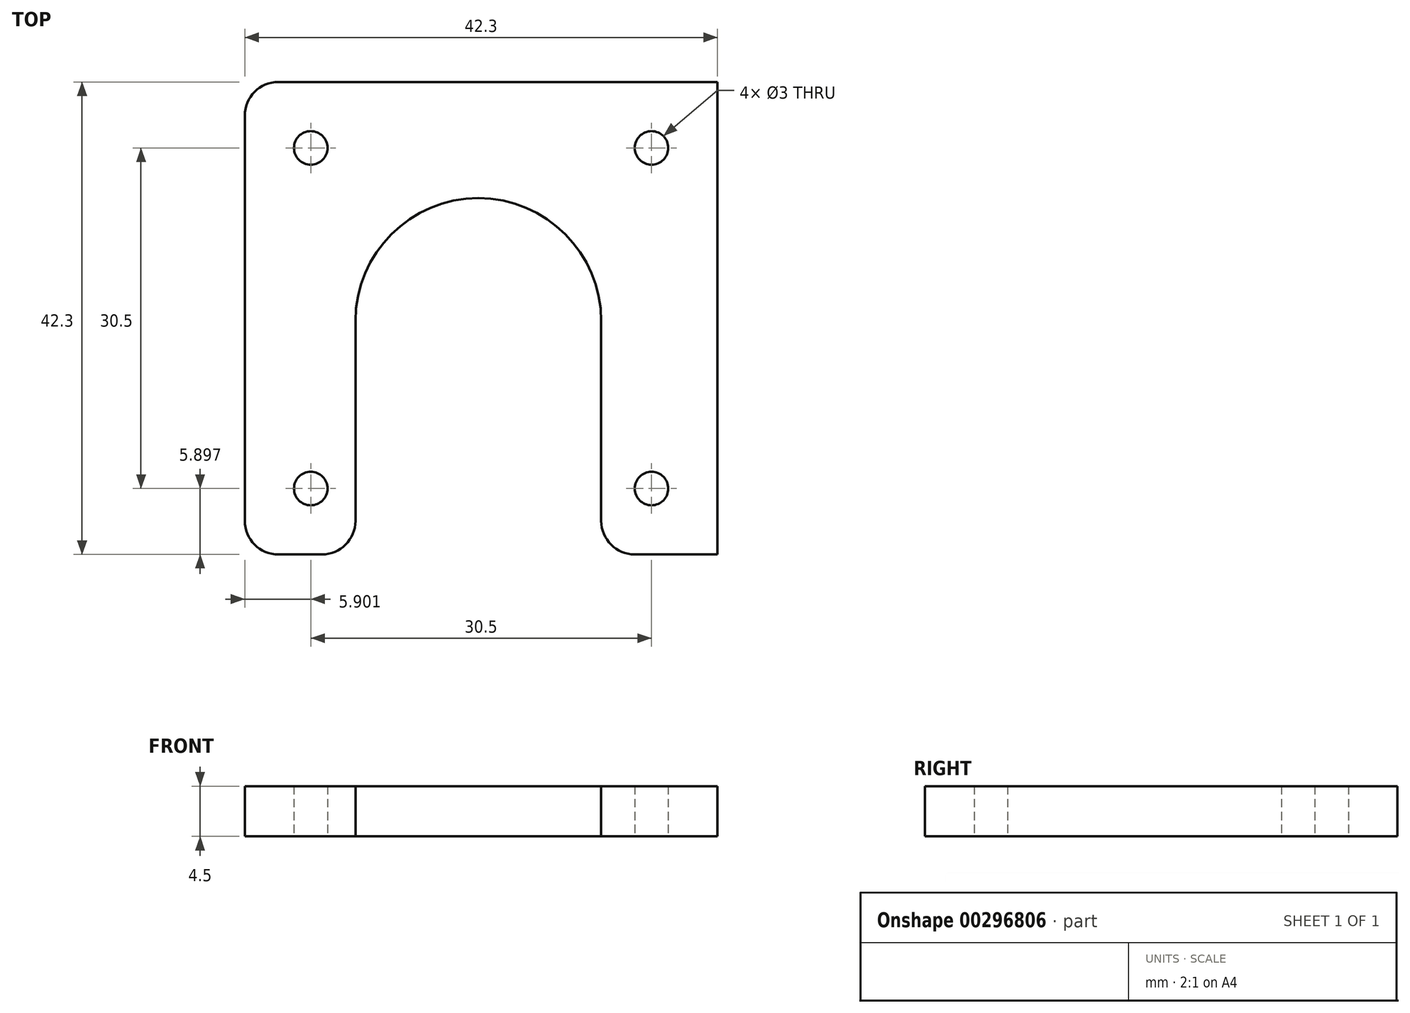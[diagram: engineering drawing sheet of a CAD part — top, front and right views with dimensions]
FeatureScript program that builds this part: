
annotation { "Feature Type Name" : "Feature", "Feature Type Description" : "" }
export const myFeature = defineFeature(function(context is Context, id is Id, definition is map)
    precondition{}
    {
        {
            var Q0;
            Q0=qCreatedBy(makeId("Top.planeOp"),FACE);
            var sketch = newSketch(context, id + "F0", { "sketchPlane" : qUnion([Q0])});
            skLineSegment(sketch, "E0.bottom", {"start": v(-20.2, 20.3) * mm, "end": v(22.1, 20.3) * mm});
            skLineSegment(sketch, "E0.top", {"start": v(-20.2, -22) * mm, "end": v(22.1, -22) * mm});
            skLineSegment(sketch, "E0.left", {"start": v(-20.2, 20.3) * mm, "end": v(-20.2, -22) * mm});
            skLineSegment(sketch, "E0.right", {"start": v(22.1, 20.3) * mm, "end": v(22.1, -22) * mm});
            skPoint(sketch, "E1", {"position": v(-14.3, 14.4) * mm});
            skPoint(sketch, "E2.0.1.0", {"position": v(-14.3, -16.1) * mm});
            skPoint(sketch, "E2.1.0.0", {"position": v(16.2, 14.4) * mm});
            skPoint(sketch, "E2.1.1.0", {"position": v(16.2, -16.1) * mm});
            skLineSegment(sketch, "E2.direction1", {"start": v(-14.3, 14.4) * mm, "end": v(16.2, 14.4) * mm, "construction": true});
            skLineSegment(sketch, "E2.direction2", {"start": v(-14.3, 14.4) * mm, "end": v(-14.3, -16.1) * mm, "construction": true});
            skCircle(sketch, "E3", {"center": v(-14.3, 14.4) * mm, "radius": 1.5 * mm});
            skCircle(sketch, "E4", {"center": v(16.2, 14.4) * mm, "radius": 1.5 * mm});
            skCircle(sketch, "E5", {"center": v(16.2, -16.1) * mm, "radius": 1.5 * mm});
            skCircle(sketch, "E6", {"center": v(-14.3, -16.1) * mm, "radius": 1.5 * mm});
            skCircle(sketch, "E7", {"center": v(0.7, -1.1) * mm, "radius": 2.5 * mm});
            skCircle(sketch, "E8", {"center": v(0.7, -1.1) * mm, "radius": 3.5 * mm, "construction": true});
            skArc(sketch, "E9", {"start": v(11.7, -1.1) * mm, "mid": v(0.7, 9.9) * mm, "end": v(-10.3, -1.1) * mm});
            skLineSegment(sketch, "E10", {"start": v(11.7, -1.1) * mm, "end": v(11.7, -22) * mm});
            skLineSegment(sketch, "E11", {"start": v(-10.3, -1.1) * mm, "end": v(-10.3, -22) * mm});
            skSolve(sketch);
        }
        {
            var Q0;
            Q0=makeQuery(id+"F0.imprint","IMPRINT",FACE,{"disambiguationData":[TD([[makeQuery(id+"F0.imprint","IMPRINT",EDGE,{"derivedFrom":sQuery(id+"F0.wireOp",EDGE,"E0.bottom")}),-1.0]])]});
            extrude(context, id + "F1", {"entities" : qUnion([Q0]), "depth" : 4.5 * mm});
        }
        {
            var Q0;
            Q0=makeQuery(id+"F1.opExtrude","SWEPT_EDGE",EDGE,{"disambiguationData":[OSD([sQuery(id+"F0.wireOp",EDGE,"E0.top"),sQuery(id+"F0.wireOp",EDGE,"E10")])]});
            var Q1;
            Q1=makeQuery(id+"F1.opExtrude","SWEPT_EDGE",EDGE,{"disambiguationData":[OSD([sQuery(id+"F0.wireOp",EDGE,"E0.top"),sQuery(id+"F0.wireOp",EDGE,"E11")])]});
            var Q2;
            Q2=makeQuery(id+"F1.opExtrude","SWEPT_EDGE",EDGE,{"disambiguationData":[OSD([sQuery(id+"F0.wireOp",EDGE,"E0.top"),sQuery(id+"F0.wireOp",EDGE,"E0.left")])]});
            var Q3;
            Q3=makeQuery(id+"F1.opExtrude","SWEPT_EDGE",EDGE,{"disambiguationData":[OSD([sQuery(id+"F0.wireOp",EDGE,"E0.bottom"),sQuery(id+"F0.wireOp",EDGE,"E0.left")])]});
            fillet(context, id + "F2", {"entities" : qUnion([Q0, Q1, Q2, Q3]), "radius" : 3 * mm, "tangentPropagation" : true, "allowEdgeOverflow" : false});
        }
    });
